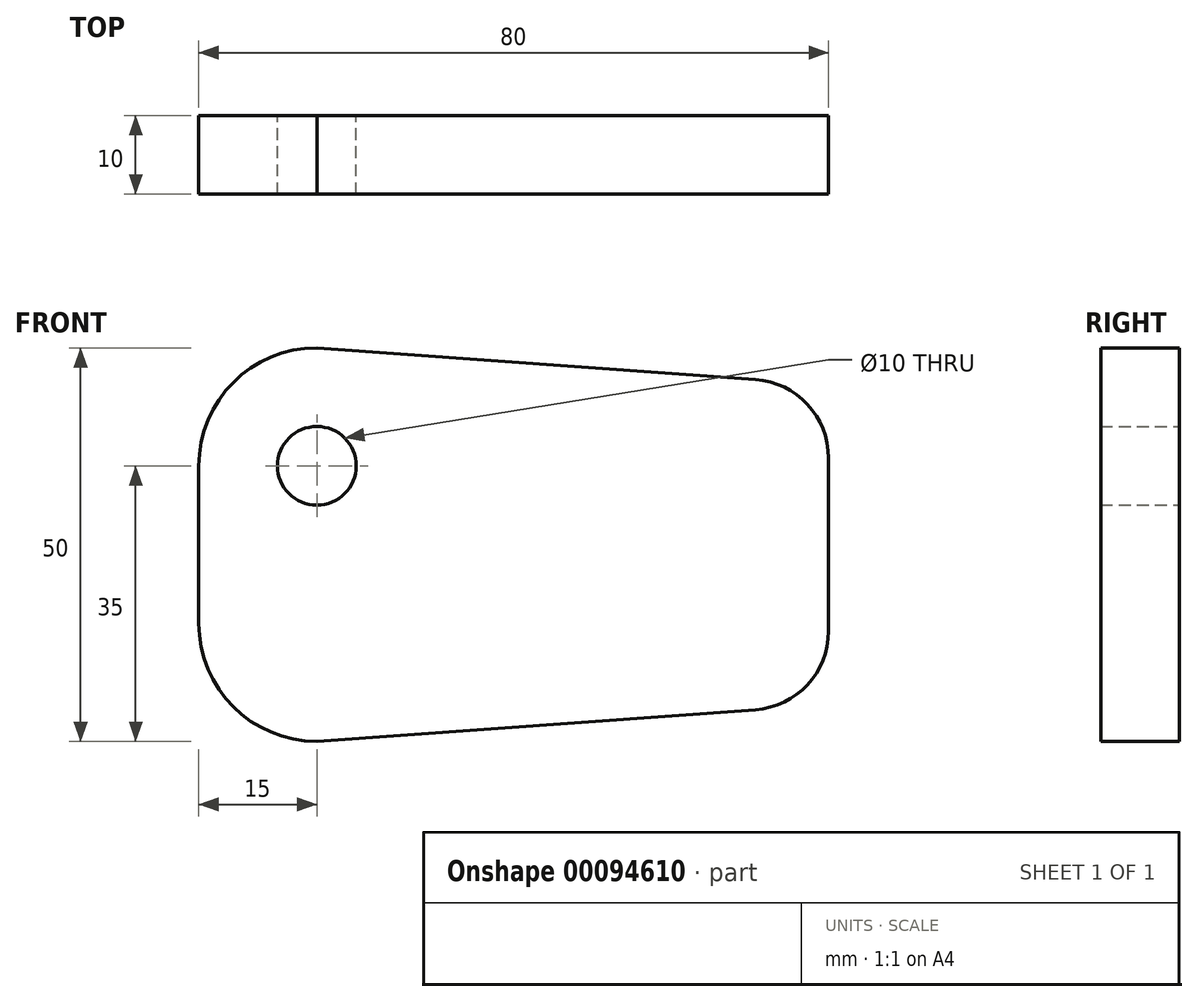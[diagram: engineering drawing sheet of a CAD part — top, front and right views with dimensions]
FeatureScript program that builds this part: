
annotation { "Feature Type Name" : "Feature", "Feature Type Description" : "" }
export const myFeature = defineFeature(function(context is Context, id is Id, definition is map)
    precondition{}
    {
        {
            var Q0;
            Q0=qCreatedBy(makeId("Front.planeOp"),FACE);
            var sketch = newSketch(context, id + "F0", { "sketchPlane" : qUnion([Q0])});
            skLineSegment(sketch, "E0", {"start": v(-72.48, 0) * mm, "end": v(71.33, 0) * mm, "construction": true});
            skLineSegment(sketch, "E1", {"start": v(0, 72.97) * mm, "end": v(0, -71.23) * mm, "construction": true});
            skCircle(sketch, "E2", {"center": v(0, 0) * mm, "radius": 15 * mm});
            skCircle(sketch, "E3", {"center": v(-25, -10) * mm, "radius": 5 * mm});
            skCircle(sketch, "E4.MirrorC", {"center": v(-25, 10) * mm, "radius": 5 * mm});
            skCircle(sketch, "E5", {"center": v(25, 0) * mm, "radius": 4 * mm});
            skLineSegment(sketch, "E6.right", {"start": v(-40, -10) * mm, "end": v(-40, 10) * mm});
            skArc(sketch, "E7.filletArc", {"start": v(-25, 25) * mm, "mid": v(-35.6, 20.6) * mm, "end": v(-40, 10) * mm});
            skArc(sketch, "E8.filletArc", {"start": v(-40, -10) * mm, "mid": v(-35.6, -20.6) * mm, "end": v(-25, -25) * mm});
            skLineSegment(sketch, "E9", {"start": v(40, 11) * mm, "end": v(40, -11) * mm});
            skArc(sketch, "E10.filletArc", {"start": v(40, 11) * mm, "mid": v(37.32, 17.81) * mm, "end": v(30.72, 20.97) * mm});
            skArc(sketch, "E11.filletArc", {"start": v(30.72, -20.97) * mm, "mid": v(37.32, -17.81) * mm, "end": v(40, -11) * mm});
            skLineSegment(sketch, "E12", {"start": v(-25, -25) * mm, "end": v(30.72, -20.97) * mm});
            skLineSegment(sketch, "E13.MirrorCS", {"start": v(-25, 25) * mm, "end": v(30.72, 20.97) * mm});
            skSolve(sketch);
        }
        {
            var Q0;
            Q0=makeQuery(id+"F0.imprint","IMPRINT",FACE,{"disambiguationData":[TD([[makeQuery(id+"F0.imprint","IMPRINT",EDGE,{"derivedFrom":sQuery(id+"F0.wireOp",EDGE,"E5")}),1.0]])]});
            var Q1;
            Q1=makeQuery(id+"F0.imprint","IMPRINT",FACE,{"disambiguationData":[TD([[makeQuery(id+"F0.imprint","IMPRINT",EDGE,{"derivedFrom":sQuery(id+"F0.wireOp",EDGE,"E4.MirrorC")}),-1.0]])]});
            var Q2;
            Q2=makeQuery(id+"F0.imprint","IMPRINT",FACE,{"disambiguationData":[TD([[makeQuery(id+"F0.imprint","IMPRINT",EDGE,{"derivedFrom":sQuery(id+"F0.wireOp",EDGE,"E3")}),1.0]])]});
            var Q3;
            Q3=makeQuery(id+"F0.imprint","IMPRINT",FACE,{"disambiguationData":[TD([[makeQuery(id+"F0.imprint","IMPRINT",EDGE,{"derivedFrom":sQuery(id+"F0.wireOp",EDGE,"E2")}),1.0]])]});
            var Q4;
            Q4=makeQuery(id+"F0.imprint","IMPRINT",FACE,{"disambiguationData":[TD([[makeQuery(id+"F0.imprint","IMPRINT",EDGE,{"derivedFrom":sQuery(id+"F0.wireOp",EDGE,"E2")}),-1.0]])]});
            extrude(context, id + "F1", {"entities" : qUnion([Q0, Q1, Q2, Q3, Q4]), "depth" : 10 * mm});
        }
    });
